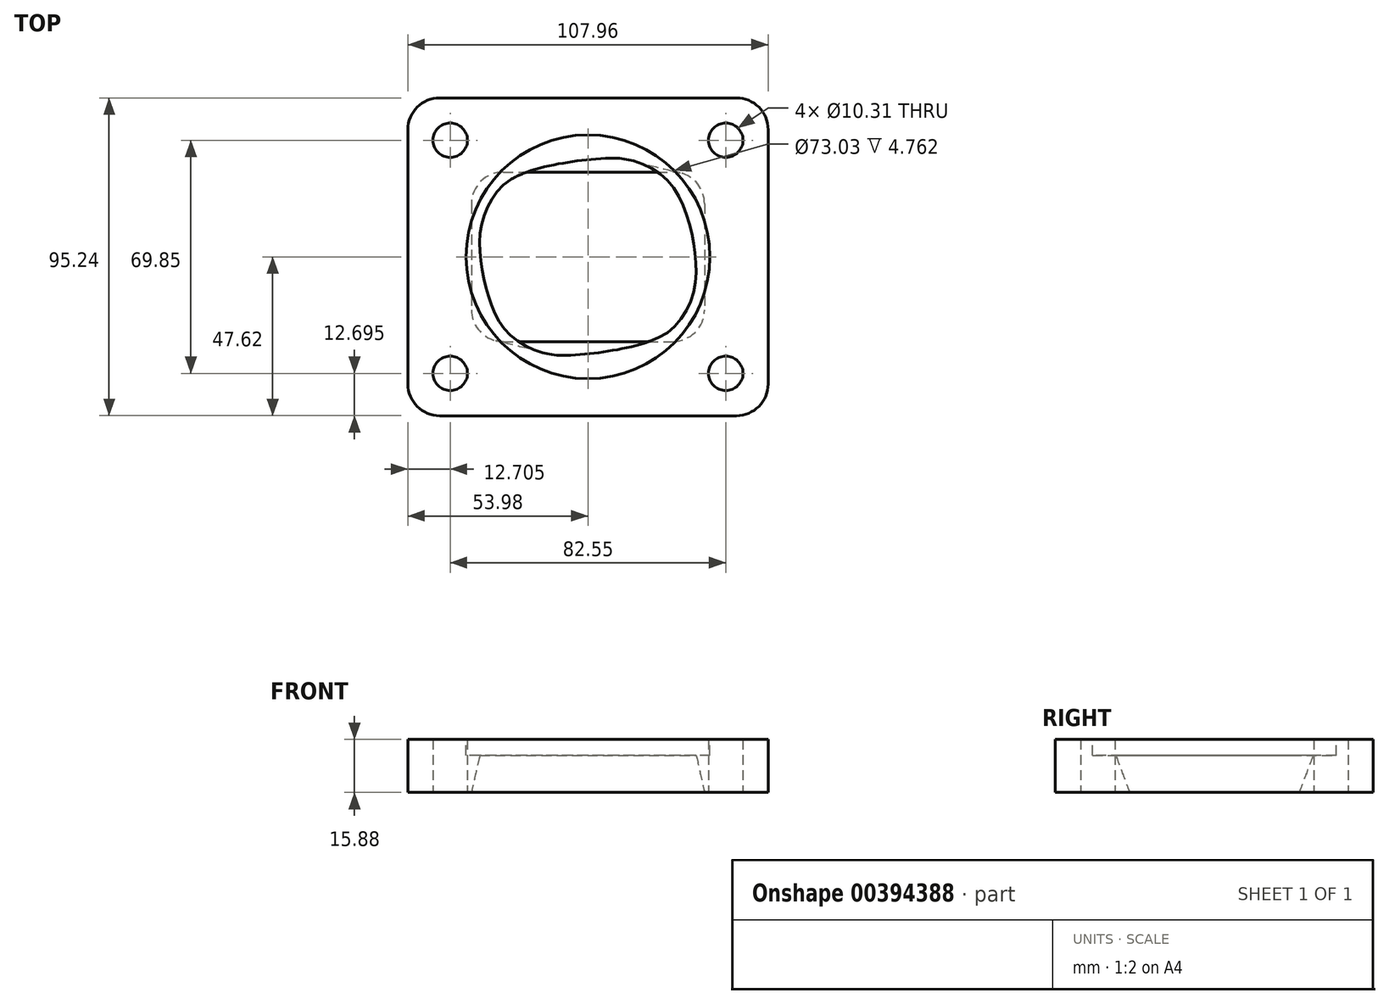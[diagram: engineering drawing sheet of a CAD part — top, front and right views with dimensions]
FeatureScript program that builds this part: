
annotation { "Feature Type Name" : "Feature", "Feature Type Description" : "" }
export const myFeature = defineFeature(function(context is Context, id is Id, definition is map)
    precondition{}
    {
        {
            var Q0;
            Q0=qCreatedBy(makeId("Top.planeOp"),FACE);
            var sketch = newSketch(context, id + "F0", { "sketchPlane" : qUnion([Q0])});
            skLineSegment(sketch, "E0.bottom", {"start": v(-44.45, -47.62) * mm, "end": v(44.45, -47.62) * mm});
            skLineSegment(sketch, "E0.top", {"start": v(-44.45, 47.63) * mm, "end": v(44.45, 47.63) * mm});
            skLineSegment(sketch, "E0.left", {"start": v(-53.97, -38.1) * mm, "end": v(-53.98, 38.1) * mm});
            skLineSegment(sketch, "E0.right", {"start": v(53.98, -38.1) * mm, "end": v(53.97, 38.1) * mm});
            skLineSegment(sketch, "E1.bottom", {"start": v(-25.4, -25.4) * mm, "end": v(25.4, -25.4) * mm});
            skLineSegment(sketch, "E1.top", {"start": v(-25.4, 25.4) * mm, "end": v(25.4, 25.4) * mm});
            skLineSegment(sketch, "E1.left", {"start": v(-34.93, -15.88) * mm, "end": v(-34.93, 15.87) * mm});
            skLineSegment(sketch, "E1.right", {"start": v(34.93, -15.87) * mm, "end": v(34.93, 15.88) * mm});
            skCircle(sketch, "E2", {"center": v(-41.27, -34.93) * mm, "radius": 5.16 * mm});
            skCircle(sketch, "E3", {"center": v(41.28, -34.93) * mm, "radius": 5.16 * mm});
            skCircle(sketch, "E4", {"center": v(41.27, 34.93) * mm, "radius": 5.16 * mm});
            skCircle(sketch, "E5", {"center": v(-41.28, 34.93) * mm, "radius": 5.16 * mm});
            skPoint(sketch, "E6.visualSharp", {"position": v(-34.92, -25.4) * mm});
            skArc(sketch, "E6.filletArc", {"start": v(-34.93, -15.88) * mm, "mid": v(-32.14, -22.61) * mm, "end": v(-25.4, -25.4) * mm});
            skPoint(sketch, "E7.visualSharp", {"position": v(-34.93, 25.4) * mm});
            skArc(sketch, "E7.filletArc", {"start": v(-25.4, 25.4) * mm, "mid": v(-32.14, 22.61) * mm, "end": v(-34.93, 15.87) * mm});
            skPoint(sketch, "E8.visualSharp", {"position": v(34.93, 25.4) * mm});
            skArc(sketch, "E8.filletArc", {"start": v(34.93, 15.88) * mm, "mid": v(32.14, 22.61) * mm, "end": v(25.4, 25.4) * mm});
            skPoint(sketch, "E9.visualSharp", {"position": v(34.93, -25.4) * mm});
            skArc(sketch, "E9.filletArc", {"start": v(25.4, -25.4) * mm, "mid": v(32.14, -22.61) * mm, "end": v(34.93, -15.87) * mm});
            skPoint(sketch, "E10.visualSharp", {"position": v(-53.97, -47.62) * mm});
            skArc(sketch, "E10.filletArc", {"start": v(-53.98, -38.1) * mm, "mid": v(-51.19, -44.84) * mm, "end": v(-44.45, -47.63) * mm});
            skPoint(sketch, "E11.visualSharp", {"position": v(53.98, -47.62) * mm});
            skArc(sketch, "E11.filletArc", {"start": v(44.45, -47.62) * mm, "mid": v(51.19, -44.84) * mm, "end": v(53.98, -38.1) * mm});
            skPoint(sketch, "E12.visualSharp", {"position": v(53.97, 47.63) * mm});
            skArc(sketch, "E12.filletArc", {"start": v(53.97, 38.1) * mm, "mid": v(51.19, 44.84) * mm, "end": v(44.45, 47.63) * mm});
            skPoint(sketch, "E13.visualSharp", {"position": v(-53.98, 47.63) * mm});
            skArc(sketch, "E13.filletArc", {"start": v(-44.45, 47.63) * mm, "mid": v(-51.19, 44.84) * mm, "end": v(-53.98, 38.1) * mm});
            skSolve(sketch);
        }
        {
            var Q0;
            Q0=qCreatedBy(makeId("Top.planeOp"),FACE);
            cPlane(context, id + "F1", {"entities" : qUnion([Q0]), "cplaneType" : CPlaneType.OFFSET, "offset" : 15.88 * mm, "width" : 152.4 * mm, "height" : 152.4 * mm});
        }
        {
            var Q0;
            Q0=qCreatedBy(id+"F1.planeOp",FACE);
            var sketch = newSketch(context, id + "F2", { "sketchPlane" : qUnion([Q0])});
            skLineSegment(sketch, "E14.bottom", {"start": v(-44.47, -47.75) * mm, "end": v(44.43, -47.75) * mm});
            skLineSegment(sketch, "E14.top", {"start": v(-44.47, 47.5) * mm, "end": v(44.43, 47.5) * mm});
            skLineSegment(sketch, "E14.left", {"start": v(-54, -38.22) * mm, "end": v(-54, 37.98) * mm});
            skLineSegment(sketch, "E14.right", {"start": v(53.95, -38.22) * mm, "end": v(53.95, 37.98) * mm});
            skCircle(sketch, "E15", {"center": v(-41.3, -35.05) * mm, "radius": 5.16 * mm});
            skCircle(sketch, "E16", {"center": v(41.25, -35.05) * mm, "radius": 5.16 * mm});
            skCircle(sketch, "E17", {"center": v(41.25, 34.8) * mm, "radius": 5.16 * mm});
            skCircle(sketch, "E18", {"center": v(-41.3, 34.8) * mm, "radius": 5.16 * mm});
            skPoint(sketch, "E19.visualSharp", {"position": v(-34.95, -25.52) * mm});
            skPoint(sketch, "E20.visualSharp", {"position": v(-34.95, 25.28) * mm});
            skPoint(sketch, "E21.visualSharp", {"position": v(34.9, 25.28) * mm});
            skPoint(sketch, "E22.visualSharp", {"position": v(34.9, -25.52) * mm});
            skPoint(sketch, "E23.visualSharp", {"position": v(-54, -47.75) * mm});
            skArc(sketch, "E23.filletArc", {"start": v(-54, -38.22) * mm, "mid": v(-51.2, -44.96) * mm, "end": v(-44.47, -47.75) * mm});
            skPoint(sketch, "E24.visualSharp", {"position": v(53.95, -47.75) * mm});
            skArc(sketch, "E24.filletArc", {"start": v(44.43, -47.75) * mm, "mid": v(51.16, -44.96) * mm, "end": v(53.95, -38.22) * mm});
            skPoint(sketch, "E25.visualSharp", {"position": v(53.95, 47.5) * mm});
            skArc(sketch, "E25.filletArc", {"start": v(53.95, 37.98) * mm, "mid": v(51.16, 44.71) * mm, "end": v(44.43, 47.5) * mm});
            skPoint(sketch, "E26.visualSharp", {"position": v(-54, 47.5) * mm});
            skArc(sketch, "E26.filletArc", {"start": v(-44.47, 47.5) * mm, "mid": v(-51.2, 44.71) * mm, "end": v(-54, 37.98) * mm});
            skCircle(sketch, "E27", {"center": v(0, 0) * mm, "radius": 31.36 * mm});
            skSolve(sketch);
        }
        {
            var Q0;
            Q0=makeQuery(id+"F0.imprint","IMPRINT",FACE,{"disambiguationData":[TD([[makeQuery(id+"F0.imprint","IMPRINT",EDGE,{"derivedFrom":sQuery(id+"F0.wireOp",EDGE,"E0.bottom")}),1.0]])]});
            var Q1;
            Q1=makeQuery(id+"F0.imprint","IMPRINT",FACE,{"disambiguationData":[TD([[makeQuery(id+"F0.imprint","IMPRINT",EDGE,{"derivedFrom":sQuery(id+"F0.wireOp",EDGE,"E1.bottom")}),1.0]])]});
            extrude(context, id + "F3", {"entities" : qUnion([Q0, Q1]), "depth" : 15.88 * mm});
        }
        {
            var Q0;
            Q0=makeQuery(id+"F3.opExtrude","CAP_FACE",FACE,{"disambiguationData":[OSD([sQuery(id+"F0.wireOp",EDGE,"E0.bottom"),sQuery(id+"F0.wireOp",EDGE,"E0.top"),sQuery(id+"F0.wireOp",EDGE,"E0.left"),sQuery(id+"F0.wireOp",EDGE,"E0.right"),sQuery(id+"F0.wireOp",EDGE,"E2"),sQuery(id+"F0.wireOp",EDGE,"E3"),sQuery(id+"F0.wireOp",EDGE,"E4"),sQuery(id+"F0.wireOp",EDGE,"E5"),sQuery(id+"F0.wireOp",EDGE,"E10.filletArc"),sQuery(id+"F0.wireOp",EDGE,"E11.filletArc"),sQuery(id+"F0.wireOp",EDGE,"E12.filletArc"),sQuery(id+"F0.wireOp",EDGE,"E13.filletArc")])],"isStart":true});
            var sketch = newSketch(context, id + "F4", { "sketchPlane" : qUnion([Q0])});
            skLineSegment(sketch, "E28.bottom", {"start": v(-25.4, -25.4) * mm, "end": v(25.4, -25.4) * mm});
            skLineSegment(sketch, "E28.top", {"start": v(-25.4, 25.4) * mm, "end": v(25.4, 25.4) * mm});
            skLineSegment(sketch, "E28.left", {"start": v(-34.93, -15.88) * mm, "end": v(-34.93, 15.87) * mm});
            skLineSegment(sketch, "E28.right", {"start": v(34.93, -15.87) * mm, "end": v(34.93, 15.88) * mm});
            skPoint(sketch, "E29.visualSharp", {"position": v(-34.92, -25.4) * mm});
            skArc(sketch, "E29.filletArc", {"start": v(-34.93, -15.88) * mm, "mid": v(-32.14, -22.61) * mm, "end": v(-25.4, -25.4) * mm});
            skArc(sketch, "E30.filletArc", {"start": v(-25.4, 25.4) * mm, "mid": v(-32.14, 22.61) * mm, "end": v(-34.93, 15.87) * mm});
            skPoint(sketch, "E31.visualSharp", {"position": v(34.93, 25.4) * mm});
            skArc(sketch, "E31.filletArc", {"start": v(34.93, 15.88) * mm, "mid": v(32.14, 22.61) * mm, "end": v(25.4, 25.4) * mm});
            skPoint(sketch, "E32.visualSharp", {"position": v(34.93, -25.4) * mm});
            skArc(sketch, "E32.filletArc", {"start": v(25.4, -25.4) * mm, "mid": v(32.14, -22.61) * mm, "end": v(34.93, -15.87) * mm});
            skSolve(sketch);
        }
        {
            var Q0;
            Q0=makeQuery(id+"F3.opExtrude","CAP_FACE",FACE,{"disambiguationData":[OSD([sQuery(id+"F0.wireOp",EDGE,"E0.bottom"),sQuery(id+"F0.wireOp",EDGE,"E0.top"),sQuery(id+"F0.wireOp",EDGE,"E0.left"),sQuery(id+"F0.wireOp",EDGE,"E0.right"),sQuery(id+"F0.wireOp",EDGE,"E2"),sQuery(id+"F0.wireOp",EDGE,"E3"),sQuery(id+"F0.wireOp",EDGE,"E4"),sQuery(id+"F0.wireOp",EDGE,"E5"),sQuery(id+"F0.wireOp",EDGE,"E10.filletArc"),sQuery(id+"F0.wireOp",EDGE,"E11.filletArc"),sQuery(id+"F0.wireOp",EDGE,"E12.filletArc"),sQuery(id+"F0.wireOp",EDGE,"E13.filletArc")])],"isStart":false});
            var sketch = newSketch(context, id + "F5", { "sketchPlane" : qUnion([Q0])});
            skCircle(sketch, "E33", {"center": v(0, 0) * mm, "radius": 36.51 * mm});
            skSolve(sketch);
        }
        {
            var Q0;
            Q0=makeQuery(id+"F5.imprint","IMPRINT",FACE,{"disambiguationData":[TD([[makeQuery(id+"F5.imprint","IMPRINT",EDGE,{"derivedFrom":sQuery(id+"F5.wireOp",EDGE,"E33")}),1.0]])]});
            extrude(context, id + "F6", {"entities" : qUnion([Q0]), "operationType" : NewBodyOperationType.REMOVE, "oppositeDirection" : true, "depth" : 4.76 * mm});
        }
        {
            var Q0;
            Q0=makeQuery(id+"F2.imprint","IMPRINT",FACE,{"disambiguationData":[TD([[makeQuery(id+"F2.imprint","IMPRINT",EDGE,{"derivedFrom":sQuery(id+"F2.wireOp",EDGE,"E27")}),1.0]])]});
            var Q1;
            Q1=makeQuery(id+"F4.imprint","IMPRINT",FACE,{"disambiguationData":[TD([[makeQuery(id+"F4.imprint","IMPRINT",EDGE,{"derivedFrom":sQuery(id+"F4.wireOp",EDGE,"E28.bottom")}),1.0]])]});
            loft(context, id + "F7", {"operationType" : NewBodyOperationType.REMOVE, "sheetProfilesArray" : [{ "sheetProfileEntities" : qUnion([Q0]) }, { "sheetProfileEntities" : qUnion([Q1]) }]});
        }
    });
